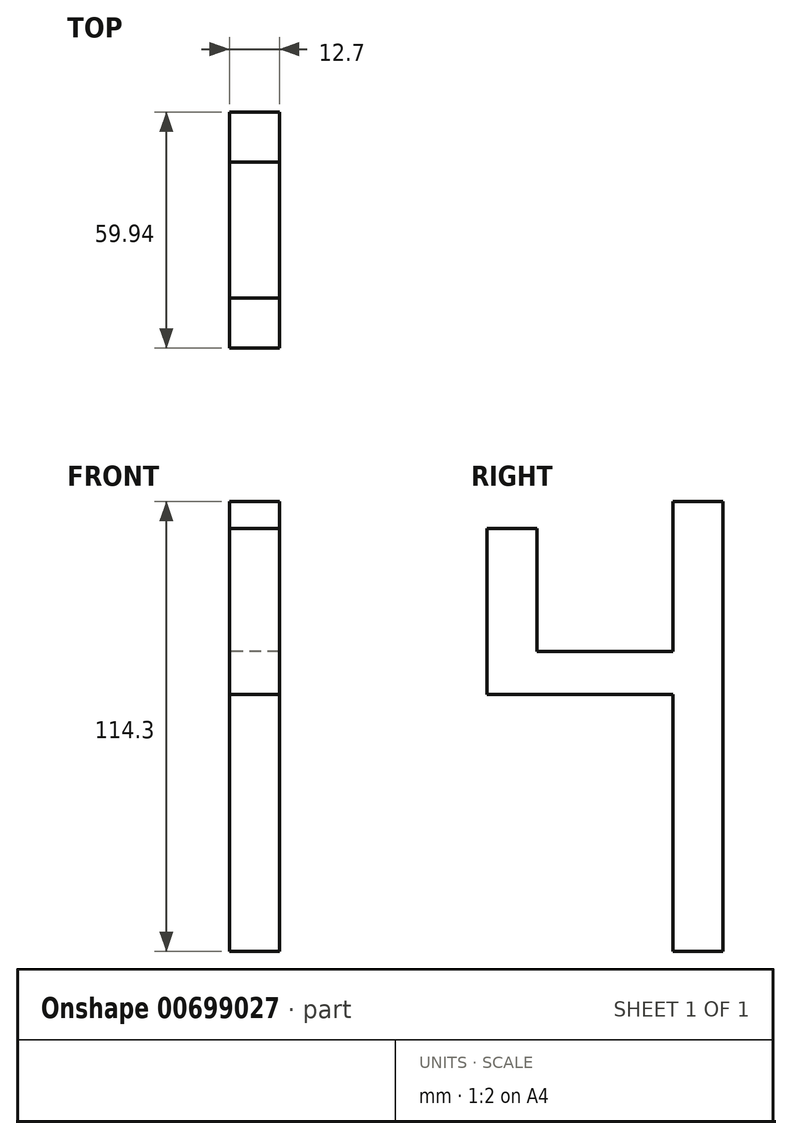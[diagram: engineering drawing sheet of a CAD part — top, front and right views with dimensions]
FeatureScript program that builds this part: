
annotation { "Feature Type Name" : "Feature", "Feature Type Description" : "" }
export const myFeature = defineFeature(function(context is Context, id is Id, definition is map)
    precondition{}
    {
        {
            var Q0;
            Q0=qCreatedBy(makeId("Front.planeOp"),FACE);
            var sketch = newSketch(context, id + "F0", { "sketchPlane" : qUnion([Q0])});
            skLineSegment(sketch, "E0.bottom", {"start": v(-38.35, -88.9) * mm, "end": v(-25.65, -88.9) * mm});
            skLineSegment(sketch, "E0.top", {"start": v(-38.35, 0) * mm, "end": v(-25.65, 0) * mm});
            skLineSegment(sketch, "E0.left", {"start": v(-38.35, -88.9) * mm, "end": v(-38.35, 0) * mm});
            skLineSegment(sketch, "E0.right", {"start": v(-25.65, -88.9) * mm, "end": v(-25.65, 0) * mm});
            skSolve(sketch);
        }
        {
            var Q0;
            Q0=makeQuery(id+"F0.imprint","IMPRINT",FACE,{"disambiguationData":[TD([[makeQuery(id+"F0.imprint","IMPRINT",EDGE,{"derivedFrom":sQuery(id+"F0.wireOp",EDGE,"E0.bottom")}),1.0]])]});
            extrude(context, id + "F1", {"entities" : qUnion([Q0]), "depth" : 12.7 * mm, "offsetDistance" : 25.4 * mm});
        }
        {
            var Q0;
            Q0=makeQuery(id+"F1.opExtrude","CAP_FACE",FACE,{"disambiguationData":[OSD([sQuery(id+"F0.wireOp",EDGE,"E0.bottom"),sQuery(id+"F0.wireOp",EDGE,"E0.top"),sQuery(id+"F0.wireOp",EDGE,"E0.left"),sQuery(id+"F0.wireOp",EDGE,"E0.right")])],"isStart":false});
            var sketch = newSketch(context, id + "F2", { "sketchPlane" : qUnion([Q0])});
            skLineSegment(sketch, "E1.bottom", {"start": v(-25.65, -23.62) * mm, "end": v(-38.35, -23.62) * mm});
            skLineSegment(sketch, "E1.top", {"start": v(-25.65, -12.66) * mm, "end": v(-38.35, -12.66) * mm});
            skLineSegment(sketch, "E1.left", {"start": v(-25.65, -23.62) * mm, "end": v(-25.65, -12.66) * mm});
            skLineSegment(sketch, "E1.right", {"start": v(-38.35, -23.62) * mm, "end": v(-38.35, -12.66) * mm});
            skSolve(sketch);
        }
        {
            var Q0;
            Q0=makeQuery(id+"F2.imprint","IMPRINT",FACE,{"disambiguationData":[TD([[makeQuery(id+"F2.imprint","IMPRINT",EDGE,{"derivedFrom":sQuery(id+"F2.wireOp",EDGE,"E1.bottom")}),-1.0]])]});
            extrude(context, id + "F3", {"entities" : qUnion([Q0]), "operationType" : NewBodyOperationType.ADD, "depth" : 30.73 * mm, "offsetDistance" : 25.4 * mm});
        }
        {
            var Q0;
            Q0=makeQuery(id+"F1.opExtrude","SWEPT_FACE",FACE,{"disambiguationData":[OSD([sQuery(id+"F0.wireOp",EDGE,"E0.top")])]});
            var sketch = newSketch(context, id + "F4", { "sketchPlane" : qUnion([Q0])});
            skLineSegment(sketch, "E2.bottom", {"start": v(-38.35, -12.7) * mm, "end": v(-25.65, -12.7) * mm});
            skLineSegment(sketch, "E2.top", {"start": v(-38.35, 0) * mm, "end": v(-25.65, 0) * mm});
            skLineSegment(sketch, "E2.left", {"start": v(-38.35, -12.7) * mm, "end": v(-38.35, 0) * mm});
            skLineSegment(sketch, "E2.right", {"start": v(-25.65, -12.7) * mm, "end": v(-25.65, 0) * mm});
            skSolve(sketch);
        }
        {
            var Q0;
            Q0=makeQuery(id+"F4.imprint","IMPRINT",FACE,{"disambiguationData":[TD([[makeQuery(id+"F4.imprint","IMPRINT",EDGE,{"derivedFrom":sQuery(id+"F4.wireOp",EDGE,"E2.bottom")}),1.0]])]});
            extrude(context, id + "F5", {"entities" : qUnion([Q0]), "operationType" : NewBodyOperationType.ADD, "depth" : 25.4 * mm, "offsetDistance" : 25.4 * mm});
        }
        {
            var Q0;
            Q0=makeQuery(id+"F3.opExtrude","CAP_FACE",FACE,{"disambiguationData":[OSD([sQuery(id+"F2.wireOp",EDGE,"E1.bottom"),sQuery(id+"F2.wireOp",EDGE,"E1.top"),sQuery(id+"F2.wireOp",EDGE,"E1.left"),sQuery(id+"F2.wireOp",EDGE,"E1.right")])],"isStart":false});
            var sketch = newSketch(context, id + "F6", { "sketchPlane" : qUnion([Q0])});
            skLineSegment(sketch, "E3.bottom", {"start": v(-38.35, -12.66) * mm, "end": v(-25.65, -12.66) * mm});
            skLineSegment(sketch, "E3.top", {"start": v(-38.35, -23.62) * mm, "end": v(-25.65, -23.62) * mm});
            skLineSegment(sketch, "E3.left", {"start": v(-38.35, -12.66) * mm, "end": v(-38.35, -23.62) * mm});
            skLineSegment(sketch, "E3.right", {"start": v(-25.65, -12.66) * mm, "end": v(-25.65, -23.62) * mm});
            skSolve(sketch);
        }
        {
            var Q0;
            Q0=makeQuery(id+"F6.imprint","IMPRINT",FACE,{"disambiguationData":[TD([[makeQuery(id+"F6.imprint","IMPRINT",EDGE,{"derivedFrom":sQuery(id+"F6.wireOp",EDGE,"E3.bottom")}),1.0]])]});
            extrude(context, id + "F7", {"entities" : qUnion([Q0]), "operationType" : NewBodyOperationType.ADD, "depth" : 16.5 * mm, "offsetDistance" : 25.4 * mm});
        }
        {
            var Q0;
            Q0=makeQuery(id+"F7.boolean.opBoolean","MERGE",FACE,{"derivedFrom":[makeQuery(id+"F3.opExtrude","SWEPT_FACE",FACE,{"disambiguationData":[OSD([sQuery(id+"F2.wireOp",EDGE,"E1.top")])]}),makeQuery(id+"F7.opExtrude","SWEPT_FACE",FACE,{"disambiguationData":[OSD([sQuery(id+"F6.wireOp",EDGE,"E3.bottom")])]})]});
            var sketch = newSketch(context, id + "F8", { "sketchPlane" : qUnion([Q0])});
            skLineSegment(sketch, "E4.bottom", {"start": v(-25.65, -59.94) * mm, "end": v(-38.35, -59.94) * mm});
            skLineSegment(sketch, "E4.top", {"start": v(-25.65, -47.24) * mm, "end": v(-38.35, -47.24) * mm});
            skLineSegment(sketch, "E4.left", {"start": v(-25.65, -59.94) * mm, "end": v(-25.65, -47.24) * mm});
            skLineSegment(sketch, "E4.right", {"start": v(-38.35, -59.94) * mm, "end": v(-38.35, -47.24) * mm});
            skSolve(sketch);
        }
        {
            var Q0;
            Q0=makeQuery(id+"F8.imprint","IMPRINT",FACE,{"disambiguationData":[TD([[makeQuery(id+"F8.imprint","IMPRINT",EDGE,{"derivedFrom":sQuery(id+"F8.wireOp",EDGE,"E4.bottom")}),-1.0]])]});
            extrude(context, id + "F9", {"entities" : qUnion([Q0]), "operationType" : NewBodyOperationType.ADD, "depth" : 31.24 * mm, "offsetDistance" : 25.4 * mm});
        }
    });
